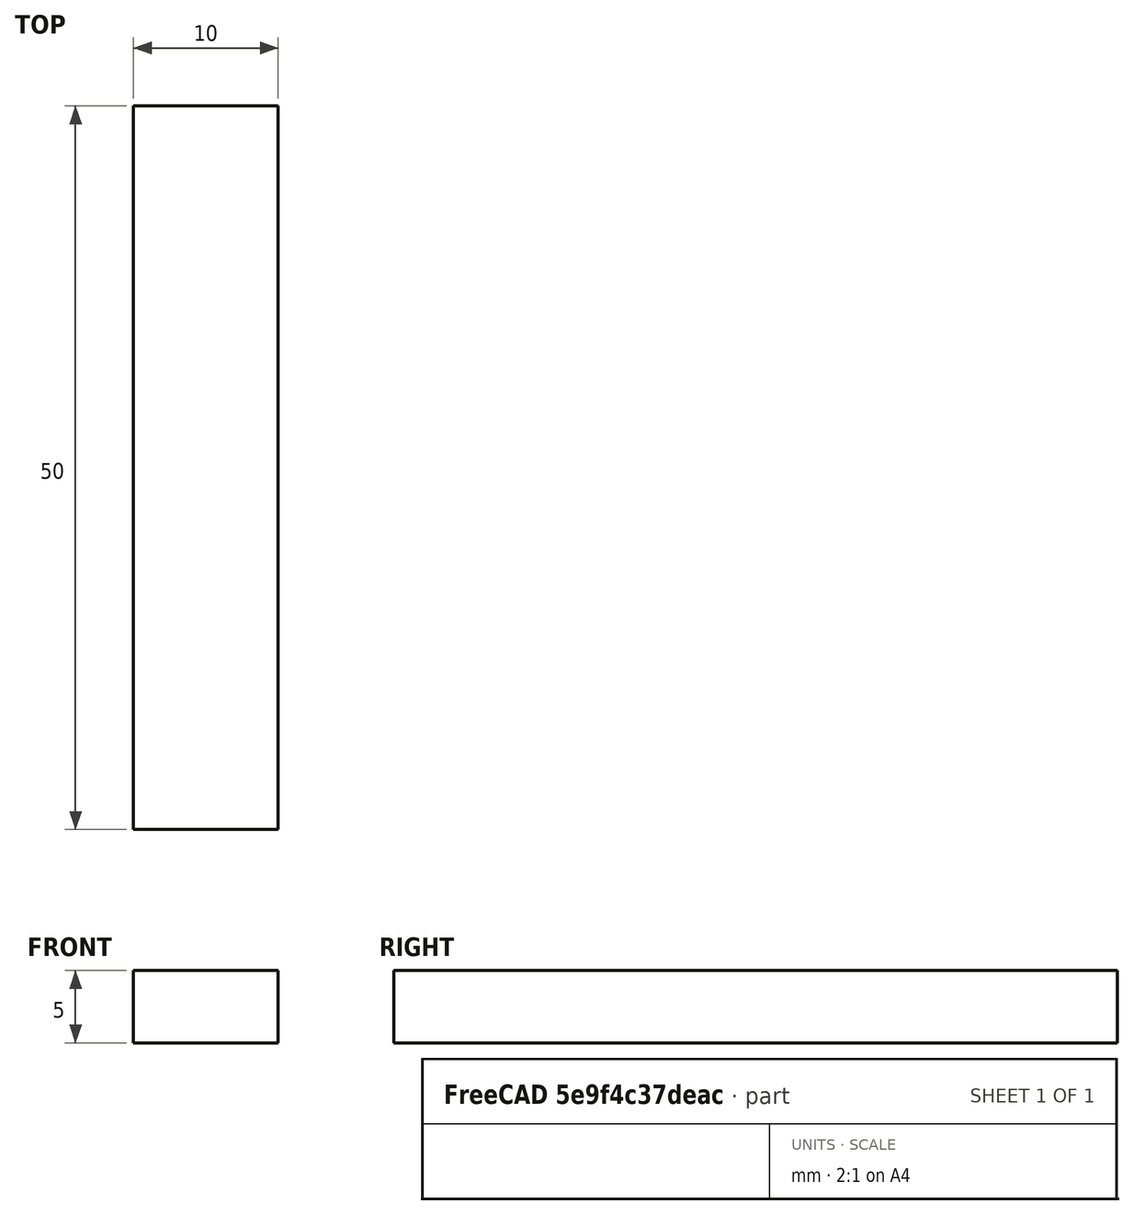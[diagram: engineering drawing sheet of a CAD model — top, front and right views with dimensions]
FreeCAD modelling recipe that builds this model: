
FCSTD DOCUMENT  (FreeCAD 0.22R35156 (Git))
Label: k1-test
License: All rights reserved
LicenseURL: https://en.wikipedia.org/wiki/All_rights_reserved
objects: Sketcher::SketchObject×1, PartDesign::Pad×1, PartDesign::Body×1
note: 4 computed .brp shape members not serialized (recipe doc carries the construction recipe); baked Part::Feature solids carry a one-line shape summary decoded from their .brp

FEATURE [Sketcher::SketchObject] Sketch
  FullyConstrained = false
  MapMode = 5
  Support = -> [XY_Plane]
  sketch-geometry (4):
    g0: LineSegment StartX=-19.6055 StartY=38.4577 StartZ=0 EndX=-19.6055 EndY=-11.5423 EndZ=0
    g1: LineSegment StartX=-19.6055 StartY=-11.5423 StartZ=0 EndX=-9.60548 EndY=-11.5423 EndZ=0
    g2: LineSegment StartX=-9.60548 StartY=-11.5423 StartZ=0 EndX=-9.60548 EndY=38.4577 EndZ=0
    g3: LineSegment StartX=-9.60548 StartY=38.4577 StartZ=0 EndX=-19.6055 EndY=38.4577 EndZ=0
  constraints (10):
    c: Coincident(g0,g1)
    c: Coincident(g1,g2)
    c: Coincident(g2,g3)
    c: Coincident(g3,g0)
    c: Vertical(g0)
    c: Vertical(g2)
    c: Horizontal(g1)
    c: Horizontal(g3)
    c: Distance(g1,g1) = 10
    c: DistanceY(g0,g0) = 50
FEATURE [PartDesign::Pad] Pad
  Direction = (0,0,1)
  Length = 5
  Length2 = 10
  Profile = -> Sketch
  ReferenceAxis = -> Sketch [N_Axis]
  Type = 0
FEATURE [PartDesign::Body] Body
  Group = -> [Sketch,Pad]
  Origin = -> Origin
  Tip = -> Pad
